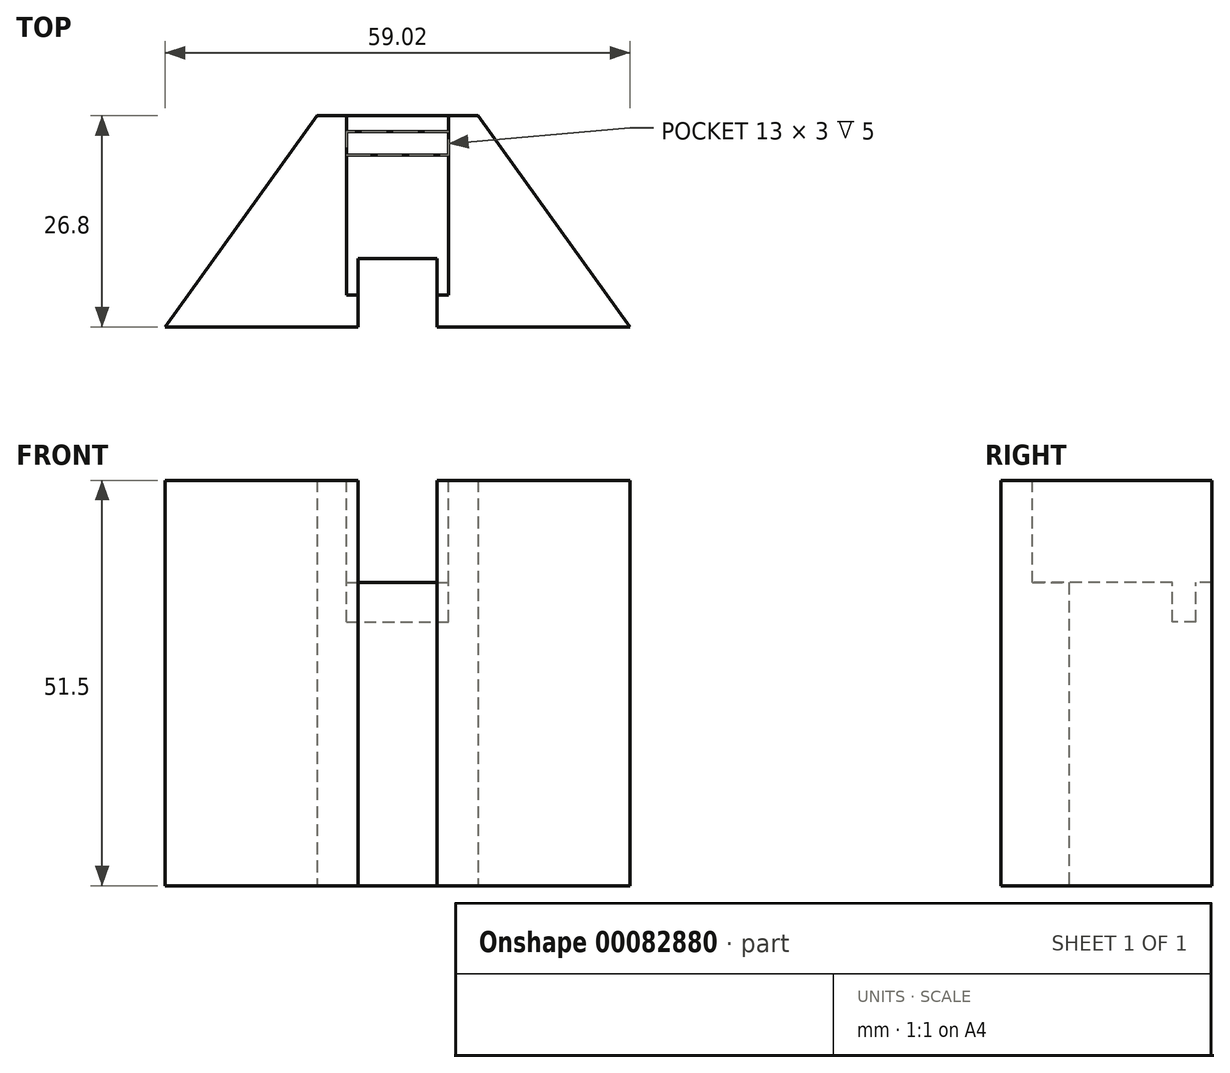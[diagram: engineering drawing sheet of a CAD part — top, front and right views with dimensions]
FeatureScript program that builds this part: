
annotation { "Feature Type Name" : "Feature", "Feature Type Description" : "" }
export const myFeature = defineFeature(function(context is Context, id is Id, definition is map)
    precondition{}
    {
        {
            var Q0;
            Q0=qCreatedBy(makeId("Top.planeOp"),FACE);
            var sketch = newSketch(context, id + "F0", { "sketchPlane" : qUnion([Q0])});
            skLineSegment(sketch, "E0", {"start": v(-29.5, 0) * mm, "end": v(-5, 0) * mm});
            skLineSegment(sketch, "E1", {"start": v(29.5, 0) * mm, "end": v(10.25, 26.8) * mm});
            skLineSegment(sketch, "E2", {"start": v(10.25, 26.8) * mm, "end": v(-10.25, 26.8) * mm});
            skLineSegment(sketch, "E3", {"start": v(-10.25, 26.8) * mm, "end": v(-29.5, 0) * mm});
            skLineSegment(sketch, "E4.top", {"start": v(5, 8.67) * mm, "end": v(-5, 8.67) * mm});
            skLineSegment(sketch, "E4.left", {"start": v(5, 0) * mm, "end": v(5, 8.67) * mm});
            skLineSegment(sketch, "E4.right", {"start": v(-5, 0) * mm, "end": v(-5, 8.67) * mm});
            skLineSegment(sketch, "E5.trimOffspring", {"start": v(5, 0) * mm, "end": v(29.5, 0) * mm});
            skSolve(sketch);
        }
        {
            var Q0;
            Q0=qSketchRegion(id+"F0",true);
            extrude(context, id + "F1", {"entities" : qUnion([Q0]), "depth" : 51.5 * mm});
        }
        {
            var Q0;
            Q0=makeQuery(id+"F1.opExtrude","CAP_FACE",FACE,{"disambiguationData":[OSD([sQuery(id+"F0.wireOp",EDGE,"E0"),sQuery(id+"F0.wireOp",EDGE,"E1"),sQuery(id+"F0.wireOp",EDGE,"E2"),sQuery(id+"F0.wireOp",EDGE,"E3"),sQuery(id+"F0.wireOp",EDGE,"E4.top"),sQuery(id+"F0.wireOp",EDGE,"E4.left"),sQuery(id+"F0.wireOp",EDGE,"E4.right"),sQuery(id+"F0.wireOp",EDGE,"E5.trimOffspring")])],"isStart":false});
            var sketch = newSketch(context, id + "F2", { "sketchPlane" : qUnion([Q0])});
            skLineSegment(sketch, "E6.bottom", {"start": v(-6.5, 26.8) * mm, "end": v(6.5, 26.8) * mm});
            skLineSegment(sketch, "E6.top", {"start": v(-6.5, 4.05) * mm, "end": v(6.5, 4.05) * mm});
            skLineSegment(sketch, "E6.left", {"start": v(-6.5, 26.8) * mm, "end": v(-6.5, 4.05) * mm});
            skLineSegment(sketch, "E6.right", {"start": v(6.5, 26.8) * mm, "end": v(6.5, 4.05) * mm});
            skSolve(sketch);
        }
        {
            var Q0;
            Q0=qSketchRegion(id+"F2",true);
            extrude(context, id + "F3", {"entities" : qUnion([Q0]), "operationType" : NewBodyOperationType.REMOVE, "oppositeDirection" : true, "depth" : 13 * mm});
        }
        {
            var Q0;
            Q0=makeQuery(id+"F3.boolean.opBoolean","COPY",FACE,{"derivedFrom":makeQuery(id+"F3.opExtrude","CAP_FACE",FACE,{"disambiguationData":[OSD([sQuery(id+"F2.wireOp",EDGE,"E6.bottom"),sQuery(id+"F2.wireOp",EDGE,"E6.top"),sQuery(id+"F2.wireOp",EDGE,"E6.left"),sQuery(id+"F2.wireOp",EDGE,"E6.right")])],"isStart":false})});
            var sketch = newSketch(context, id + "F4", { "sketchPlane" : qUnion([Q0])});
            skLineSegment(sketch, "E7.bottom", {"start": v(-6.5, 24.8) * mm, "end": v(6.5, 24.8) * mm});
            skLineSegment(sketch, "E7.top", {"start": v(-6.5, 21.8) * mm, "end": v(6.5, 21.8) * mm});
            skLineSegment(sketch, "E7.left", {"start": v(-6.5, 24.8) * mm, "end": v(-6.5, 21.8) * mm});
            skLineSegment(sketch, "E7.right", {"start": v(6.5, 24.8) * mm, "end": v(6.5, 21.8) * mm});
            skSolve(sketch);
        }
        {
            var Q0;
            Q0=qSketchRegion(id+"F4",true);
            extrude(context, id + "F5", {"entities" : qUnion([Q0]), "operationType" : NewBodyOperationType.REMOVE, "oppositeDirection" : true, "depth" : 5 * mm});
        }
    });
